# Revit family: Sink-Drop_In-Lavatory-KOHLER-Memoirs-K-2241IN
name_source: partatom
category: Plumbing Fixtures
revit_build: Autodesk Revit 2017 (Build: 20160225_1515(x64)
units: mm (PartAtom-declared; Revit-internal decimal feet)

## family parameters
Cut with Voids When Loaded = No
Host = Face
OmniClass Number = 23.31.13.00
OmniClass Title = Sinks
Part Type = Normal
Room Calculation Point = No
Round Connector Dimension = Use Diameter
Shared = No

## types (2) — shared parameters
ADA Compliant = No
Assembly Code = D2010400
CW Connection = No
Cold Water Inlet = Cold Water Inlet
Date Modified = 05/13/2020
Default Elevation = 36"
Drain Included = No
Finish = Kohler-Vitreous_China-0-White
HW Connection = No
Height = 8 11/16"
Hot Water Inlet = Hot Water Inlet
Length = 18 1/16"
Manufacturer = KOHLER Co.
Master Format 2014 = 22 41 16
Master Format 2014 Name = Residential Lavatories and Sinks
Material = Vitreous China
Product Name = Memoirs
URL = https://www.kohler.co.in
Vent Connection = No
Waste Connection = Yes
Waste Water Outlet = Waste Water Outlet
WaterSense Certified = No
Width = 22 13/16"

## per-type parameters (varying)
| type | 8_inch middle hole | Description | Model | Product Page URL | Single hole | Type |
| Single Faucet Hole, 0-White | No | Self-rimming lavatory with single faucet hole | K-2241IN-1-0 | https://www.kohler.co.in | Yes | 1 |
| 8 Inch Faucet Hole, 0-White | Yes | Self-rimming lavatory with 8 inch faucet hole | K-2241IIN-8-0 |  | No | 2 |

## geometry (parser evidence)
native form markers: Sweep x3
no freeform markers — native parametric forms only
